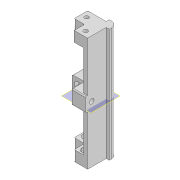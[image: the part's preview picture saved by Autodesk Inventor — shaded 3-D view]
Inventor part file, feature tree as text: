
AUTODESK INVENTOR PART (.ipt)
format: ipt  version: 2020 (Build 240168000, 168)  size: 367,104 bytes
history: native  units: mm
features: extrude x13, sketch x13, other x7, fillet x2
ambient origin geometry x8: Origin, YZ Plane, XZ Plane, XY Plane, X Axis, Y Axis, Z Axis, Center Point
bodies: Body1 (feature_tree)
feature tree (35):
  other  "Sólido1"
  extrude  "Extrusão1"  Depth=16.0mm
  extrude  "Extrusão2"  Depth=3.0mm
  extrude  "Extrusão3"  Depth=3.0mm
  extrude  "Extrusão4"  Depth=6.0mm
  extrude  "Extrusão5"  Depth=8.0mm
  fillet  "Arredondamento1"  Radius=110.0mm
  extrude  "Extrusão6"  Depth=10.0mm
  extrude  "Extrusão7"  TaperAngle=0.0deg  [1 undecoded]
  other  "Plano de trabalho1"
  extrude  "Extrusão9"  Depth=5.0mm
  extrude  "Extrusão10"  Depth=10.0mm
  extrude  "Extrusão11"  Depth=4.0mm
  extrude  "Extrusão12"  Depth=7.0mm
  extrude  "Extrusão13"  Depth=1.0mm TaperAngle=0.0deg
  fillet  "Arredondamento2"  Radius=1.0mm
  extrude  "Extrusão14"  Depth=6.95mm
  sketch  "Esboço1"  dims[d0=16.0mm d1=16.0mm]
  sketch  "Esboço2"  dims[d2=8.0mm d3=3.0mm]
  sketch  "Esboço3"  dims[d4=8.0mm d5=3.0mm]
  sketch  "Esboço4"  dims[d6=6.0mm d7=5.2mm]
  sketch  "Esboço5"  dims[d8=8.0mm d9=8.0mm d10=110.0mm d11=0.0mm]
  sketch  "Esboço6"  dims[d12=10.0mm d13=10.0mm]
  sketch  "Esboço7"  dims[d14=10.0mm d15=0.0mm d16=0.0mm]
  other  "Contorno projetado1"
  other  "Contorno projetado2"
  sketch  "Esboço9"  dims[d17=4.0mm d18=5.0mm]
  other  "Contorno projetado3"
  other  "Contorno projetado4"
  sketch  "Esboço10"  dims[d19=200.0mm d20=0.0mm d21=10.0mm]
  sketch  "Esboço11"  dims[d22=10.0mm d23=0.0mm d24=4.0mm]
  sketch  "Esboço12"  dims[d25=5.0mm d26=7.0mm]
  sketch  "Esboço13"  dims[d27=6.0mm d28=200.0mm d29=0.0mm d30=1.0mm]
  sketch  "Esboço14"  dims[d31=13.0mm d32=6.95mm d33=6.95mm d34=4.0mm d35=0.0mm d36=4.0mm d37=0.0mm d38=0.0mm d44=0.0mm d45=-50.0mm d46=12.0mm d47=12.0mm d48=2.0mm d49=0.0mm d50=12.0mm d51=0.0mm d52=4.5mm d53=6.0mm d54=20.0mm d55=0.0mm d56=4.5mm d57=6.0mm d58=20.0mm d59=0.0mm d60=6.95mm d61=4.0mm d62=0.0mm d63=6.95mm d64=4.0mm d65=0.0mm d66=1.0mm d67=4.0mm d68=0.0mm]
  other  "Contorno projetado5"
note: 1 required parameter value undecoded (feature->parameter linkage not recoverable at this tier; creation-order binding heuristic only, values carry confidence <= 0.55)
